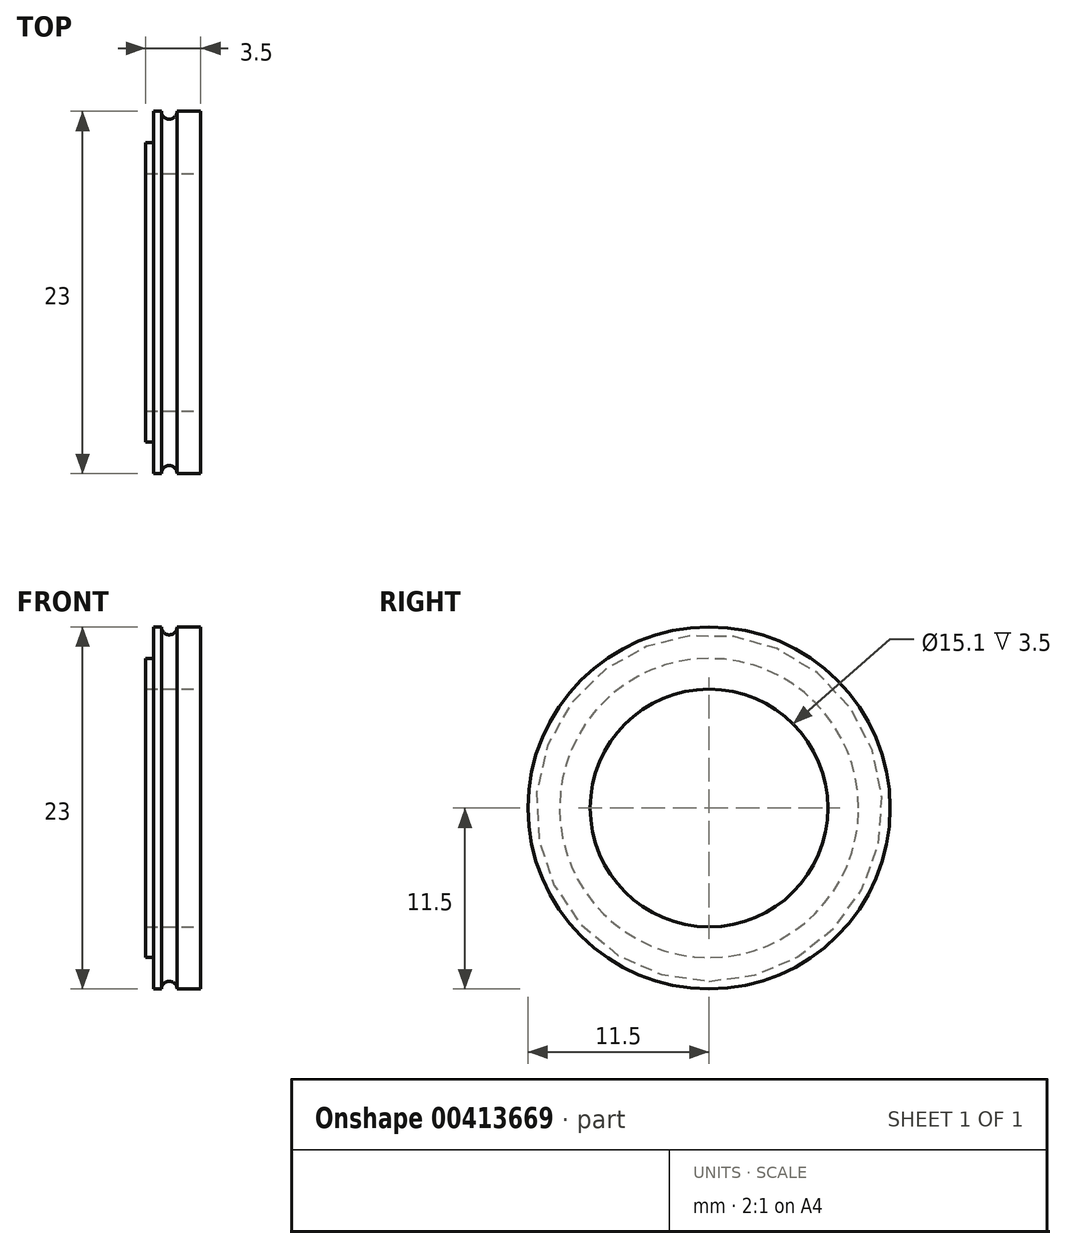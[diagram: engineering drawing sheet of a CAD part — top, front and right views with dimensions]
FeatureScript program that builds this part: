
annotation { "Feature Type Name" : "Feature", "Feature Type Description" : "" }
export const myFeature = defineFeature(function(context is Context, id is Id, definition is map)
    precondition{}
    {
        {
            var Q0;
            Q0=qCreatedBy(makeId("Right.planeOp"),FACE);
            var sketch = newSketch(context, id + "F0", { "sketchPlane" : qUnion([Q0])});
            skCircle(sketch, "E0", {"center": v(0, 0) * mm, "radius": 11.5 * mm});
            skSolve(sketch);
        }
        {
            var Q0;
            Q0=makeQuery(id+"F0.imprint","IMPRINT",FACE,{"disambiguationData":[TD([[makeQuery(id+"F0.imprint","IMPRINT",EDGE,{"derivedFrom":sQuery(id+"F0.wireOp",EDGE,"E0")}),1.0]])]});
            extrude(context, id + "F1", {"entities" : qUnion([Q0]), "depth" : 3 * mm, "offsetDistance" : 25 * mm});
        }
        {
            var Q0;
            Q0=makeQuery(id+"F1.opExtrude","CAP_FACE",FACE,{"disambiguationData":[OSD([sQuery(id+"F0.wireOp",EDGE,"E0")])],"isStart":true});
            var sketch = newSketch(context, id + "F2", { "sketchPlane" : qUnion([Q0])});
            skCircle(sketch, "E1", {"center": v(0, 0) * mm, "radius": 9.5 * mm});
            skSolve(sketch);
        }
        {
            var Q0;
            Q0=makeQuery(id+"F2.imprint","IMPRINT",FACE,{"disambiguationData":[TD([[makeQuery(id+"F2.imprint","IMPRINT",EDGE,{"derivedFrom":sQuery(id+"F2.wireOp",EDGE,"E1")}),1.0]])]});
            extrude(context, id + "F3", {"entities" : qUnion([Q0]), "operationType" : NewBodyOperationType.ADD, "depth" : 0.5 * mm, "offsetDistance" : 25 * mm});
        }
        {
            var Q0;
            Q0=makeQuery(id+"F3.opExtrude","CAP_FACE",FACE,{"disambiguationData":[OSD([sQuery(id+"F2.wireOp",EDGE,"E1")])],"isStart":false});
            var sketch = newSketch(context, id + "F4", { "sketchPlane" : qUnion([Q0])});
            skPoint(sketch, "E2", {"position": v(0, 0) * mm});
            skSolve(sketch);
        }
        {
            var Q0;
            Q0=sQuery(id+"F4.wireOp",VERTEX,"E2");
            var Q1;
            Q1=makeQuery(id+"F1.opExtrude","SWEPT_BODY",BODY,{"disambiguationData":[OSD([sQuery(id+"F0.wireOp",EDGE,"E0")])]});
            hole(context, id + "F5", {"style" : HoleStyle.SIMPLE, "endStyle" : HoleEndStyle.BLIND, "holeDiameter" : 15.1 * mm, "majorDiameter" : 5 * mm, "holeDepth" : 30 * mm, "isTappedThrough" : true, "tappedDepth" : 12 * mm, "tapClearance" : 3, "locations" : qUnion([Q0]), "scope" : qUnion([Q1]), "startStyle" : HoleStartStyle.SKETCH});
        }
        {
            var Q0;
            Q0=qCreatedBy(makeId("Front.planeOp"),FACE);
            var sketch = newSketch(context, id + "F6", { "sketchPlane" : qUnion([Q0])});
            skCircle(sketch, "E3", {"center": v(1, -11.5) * mm, "radius": 0.5 * mm});
            skSolve(sketch);
        }
        {
            var Q0;
            Q0=makeQuery(id+"F6.imprint","IMPRINT",FACE,{"disambiguationData":[TD([[makeQuery(id+"F6.imprint","IMPRINT",EDGE,{"derivedFrom":sQuery(id+"F6.wireOp",EDGE,"E3")}),1.0]])]});
            var Q1;
            Q1=makeQuery(id+"F1.opExtrude","CAP_EDGE",EDGE,{"disambiguationData":[OSD([sQuery(id+"F0.wireOp",EDGE,"E0")])],"isStart":true});
            sweep(context, id + "F7", {"operationType" : NewBodyOperationType.REMOVE, "profiles" : qUnion([Q0]), "path" : qUnion([Q1])});
        }
    });
